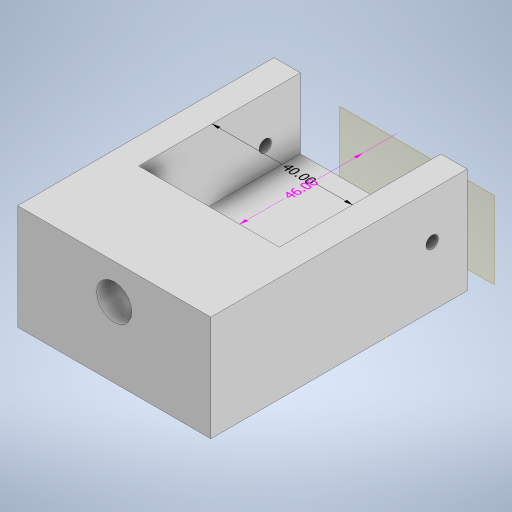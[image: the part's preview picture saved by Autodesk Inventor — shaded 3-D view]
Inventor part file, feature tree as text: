
AUTODESK INVENTOR PART (.ipt)
format: ipt  version: 2023 (Build 270158000, 158)  size: 296,960 bytes
history: native  units: mm
features: sketch x8, extrude x6, other x4, plane x3, hole x1, split x1
ambient origin geometry x8: Origin, YZ Plane, XZ Plane, XY Plane, X Axis, Y Axis, Z Axis, Center Point
bodies: Body1 (feature_tree)
feature tree (23):
  other  "Sólido1"
  other  "Anotaciones"
  extrude  "Extrusión1"  Depth=55.0mm
  extrude  "Extrusión2"  Depth=10.0mm
  extrude  "Extrusión3"  Depth=5.0mm
  extrude  "Extrusión4"  Depth=10.0mm TaperAngle=0.0deg
  plane  "Plano de trabajo1"
  extrude  "Extrusión5"  Depth=10.0mm
  plane  "Plano de trabajo2"
  extrude  "Extrusión6"  Depth=40.0mm
  sketch  "Boceto7"  dims[d15=46.0mm d16=20.0mm d17=0.0mm]
  plane  "Plano de trabajo4"
  hole  "Agujero1"  [1 undecoded]
  split  "Dividir1"
  sketch  "Boceto1"  dims[d0=55.0mm d1=100.0mm]
  sketch  "Boceto2"  dims[d2=30.0mm d3=0.0mm d4=10.0mm]
  sketch  "Boceto3"  dims[d5=20.0mm d6=5.0mm]
  sketch  "Boceto4"  dims[d7=22.5mm d8=10.0mm d9=0.0mm]
  sketch  "Boceto5"  dims[d10=10.0mm d11=10.0mm]
  sketch  "Boceto6"  dims[d12=15.0mm d13=0.0mm d14=40.0mm]
  sketch  "Boceto8"  dims[d24=22.5mm d25=2.5mm d26=2.5mm d27=8.0mm d28=0.0mm d29=3.0mm d30=3.0mm d31=8.0mm d32=0.0mm d33=0.0mm d34=10.0mm d35=30.0mm d36=5.0mm d37=5.0mm d38=5.0mm d39=5.0mm d40=10.0mm d41=8.0mm d42=3.5mm d43=6.0mm d44=4.0mm d45=2.0mm d46=90.0deg d47=8.0mm d48=20.594885mm d18=5.462798mm d19=4.90751mm d20=46.0mm d21=4.68859mm d22=6.124374mm d23=40.0mm]
  other  "Cota lineal 1"
  other  "Cota lineal 2"
note: 1 required parameter value undecoded (feature->parameter linkage not recoverable at this tier; creation-order binding heuristic only, values carry confidence <= 0.55)
